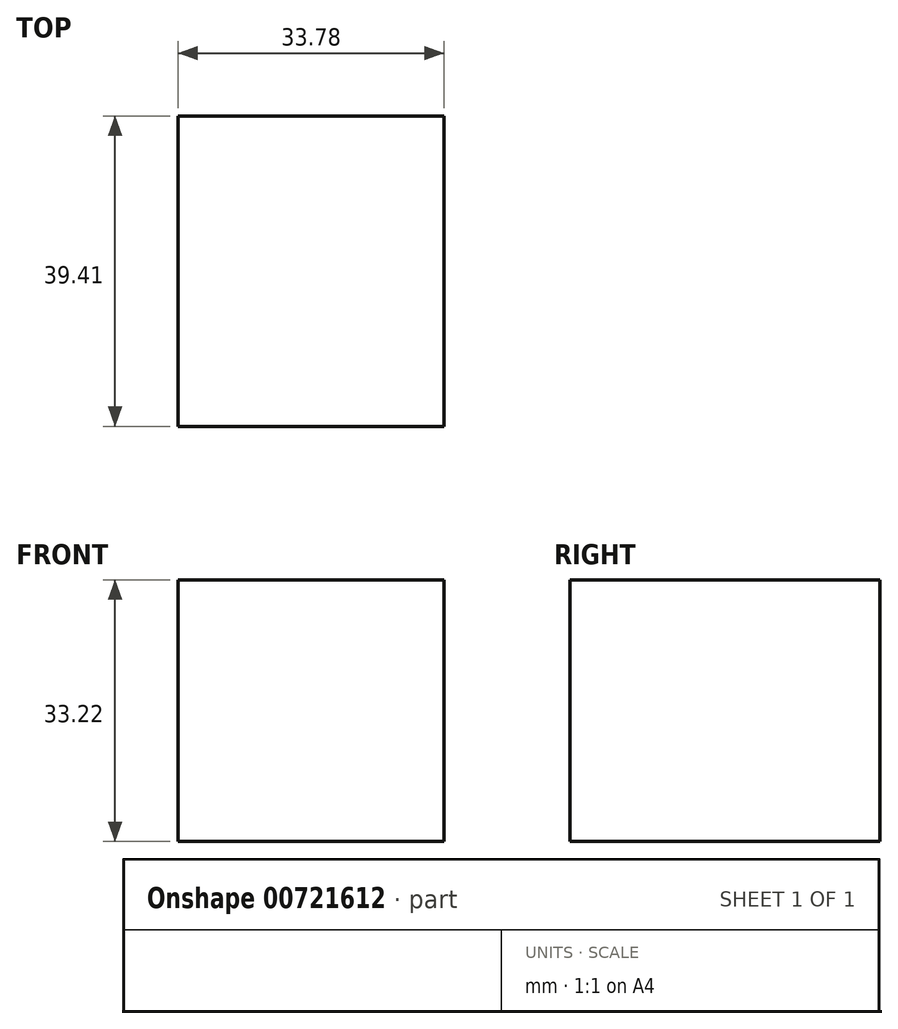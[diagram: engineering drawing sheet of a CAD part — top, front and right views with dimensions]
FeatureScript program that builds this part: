
annotation { "Feature Type Name" : "Feature", "Feature Type Description" : "" }
export const myFeature = defineFeature(function(context is Context, id is Id, definition is map)
    precondition{}
    {
        {
            var Q0;
            Q0=qCreatedBy(makeId("Right.planeOp"),FACE);
            var sketch = newSketch(context, id + "F0", { "sketchPlane" : qUnion([Q0])});
            skLineSegment(sketch, "E0.bottom", {"start": v(-39.4, 33.22) * mm, "end": v(0, 33.22) * mm});
            skLineSegment(sketch, "E0.top", {"start": v(-39.4, 0) * mm, "end": v(0, 0) * mm});
            skLineSegment(sketch, "E0.left", {"start": v(-39.4, 33.22) * mm, "end": v(-39.4, 0) * mm});
            skLineSegment(sketch, "E0.right", {"start": v(0, 33.22) * mm, "end": v(0, 0) * mm});
            skSolve(sketch);
        }
        {
            var Q0;
            Q0=makeQuery(id+"F0.imprint","IMPRINT",FACE,{"disambiguationData":[TD([[makeQuery(id+"F0.imprint","IMPRINT",EDGE,{"derivedFrom":sQuery(id+"F0.wireOp",EDGE,"E0.bottom")}),-1.0]])]});
            extrude(context, id + "F1", {"entities" : qUnion([Q0]), "depth" : 33.78 * mm, "offsetDistance" : 25.4 * mm});
        }
    });
